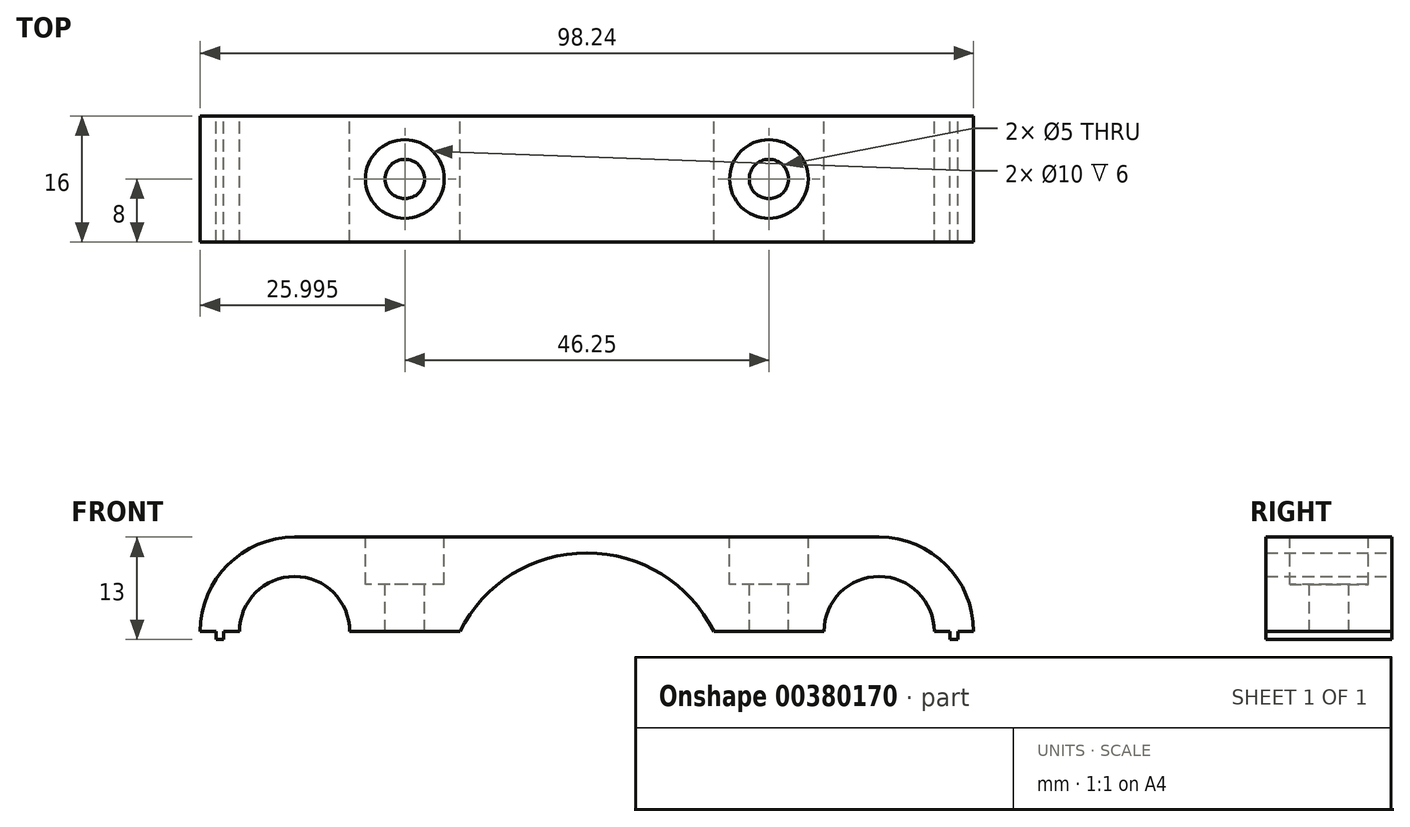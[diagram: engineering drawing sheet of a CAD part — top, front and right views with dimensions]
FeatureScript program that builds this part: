
annotation { "Feature Type Name" : "Feature", "Feature Type Description" : "" }
export const myFeature = defineFeature(function(context is Context, id is Id, definition is map)
    precondition{}
    {
        {
            var Q0;
            Q0=qCreatedBy(makeId("Front.planeOp"),FACE);
            var sketch = newSketch(context, id + "F0", { "sketchPlane" : qUnion([Q0])});
            skLineSegment(sketch, "E0", {"start": v(-44.12, -6) * mm, "end": v(-49.12, -6) * mm});
            skLineSegment(sketch, "E1", {"start": v(-49.12, -6) * mm, "end": v(-49.12, 6) * mm});
            skLineSegment(sketch, "E2", {"start": v(-49.12, 6) * mm, "end": v(49.12, 6) * mm});
            skLineSegment(sketch, "E3", {"start": v(49.12, 6) * mm, "end": v(49.12, -6) * mm});
            skLineSegment(sketch, "E4", {"start": v(49.12, -6) * mm, "end": v(44.12, -6) * mm});
            skArc(sketch, "E5", {"start": v(44.13, -6) * mm, "mid": v(37.13, 1) * mm, "end": v(30.12, -6) * mm});
            skArc(sketch, "E6", {"start": v(-30.12, -6) * mm, "mid": v(-37.12, 1) * mm, "end": v(-44.12, -6) * mm});
            skArc(sketch, "E7", {"start": v(16.12, -6) * mm, "mid": v(0, 4) * mm, "end": v(-16.12, -6) * mm});
            skLineSegment(sketch, "E8", {"start": v(-30.12, -6) * mm, "end": v(-16.12, -6) * mm});
            skLineSegment(sketch, "E9", {"start": v(16.12, -6) * mm, "end": v(30.12, -6) * mm});
            skSolve(sketch);
        }
        {
            var Q0;
            Q0=makeQuery(id+"F0.imprint","IMPRINT",FACE,{"disambiguationData":[TD([[makeQuery(id+"F0.imprint","IMPRINT",EDGE,{"derivedFrom":sQuery(id+"F0.wireOp",EDGE,"E0")}),-1.0]])]});
            extrude(context, id + "F1", {"entities" : qUnion([Q0]), "endBound" : BoundingType.SYMMETRIC, "depth" : 16 * mm});
        }
        {
            var Q0;
            Q0=makeQuery(id+"F1.opExtrude","SWEPT_FACE",FACE,{"disambiguationData":[OSD([sQuery(id+"F0.wireOp",EDGE,"E2")])]});
            var sketch = newSketch(context, id + "F2", { "sketchPlane" : qUnion([Q0])});
            skPoint(sketch, "E10", {"position": v(-23.12, 0) * mm});
            skPoint(sketch, "E11", {"position": v(23.12, 0) * mm});
            skSolve(sketch);
        }
        {
            var Q0;
            Q0=sQuery(id+"F2.wireOp",VERTEX,"c18a094e-cac8-44d5-8395-e5b24407ddbc");
            var Q1;
            Q1=sQuery(id+"F2.wireOp",VERTEX,"E10");
            var Q2;
            Q2=sQuery(id+"F2.wireOp",VERTEX,"E11");
            var Q3;
            Q3=sQuery(id+"F2.wireOp",VERTEX,"e4976973-dec0-4e5f-b838-203971ea5778");
            var Q4;
            Q4=makeQuery(id+"F1.opExtrude","SWEPT_BODY",BODY,{"disambiguationData":[OSD([sQuery(id+"F0.wireOp",EDGE,"E0"),sQuery(id+"F0.wireOp",EDGE,"E1"),sQuery(id+"F0.wireOp",EDGE,"E2"),sQuery(id+"F0.wireOp",EDGE,"E3"),sQuery(id+"F0.wireOp",EDGE,"E4"),sQuery(id+"F0.wireOp",EDGE,"E5"),sQuery(id+"F0.wireOp",EDGE,"E6"),sQuery(id+"F0.wireOp",EDGE,"IZRTLZFC-gH6G-mexX-SaW8-7kCsowfcQd4H")])]});
            hole(context, id + "F3", {"style" : HoleStyle.C_BORE, "endStyle" : HoleEndStyle.THROUGH, "holeDiameter" : 5 * mm, "cBoreDiameter" : 10 * mm, "cBoreDepth" : 6 * mm, "isTappedThrough" : true, "tappedDepth" : 12.7 * mm, "tapClearance" : 3, "locations" : qUnion([Q0, Q1, Q2, Q3]), "scope" : qUnion([Q4])});
        }
        {
            var Q0;
            Q0=makeQuery(id+"F1.opExtrude","SWEPT_EDGE",EDGE,{"disambiguationData":[OSD([sQuery(id+"F0.wireOp",EDGE,"E2"),sQuery(id+"F0.wireOp",EDGE,"E3")])]});
            var Q1;
            Q1=makeQuery(id+"F1.opExtrude","SWEPT_EDGE",EDGE,{"disambiguationData":[OSD([sQuery(id+"F0.wireOp",EDGE,"E1"),sQuery(id+"F0.wireOp",EDGE,"E2")])]});
            fillet(context, id + "F4", {"entities" : qUnion([Q0, Q1]), "radius" : 12 * mm, "tangentPropagation" : true, "allowEdgeOverflow" : false});
        }
        {
            var Q0;
            Q0=makeQuery(id+"F1.opExtrude","SWEPT_FACE",FACE,{"disambiguationData":[OSD([sQuery(id+"F0.wireOp",EDGE,"E0")])]});
            var sketch = newSketch(context, id + "F5", { "sketchPlane" : qUnion([Q0])});
            skLineSegment(sketch, "E12.bottom", {"start": v(-47.12, 8) * mm, "end": v(-46.12, 8) * mm});
            skLineSegment(sketch, "E12.top", {"start": v(-47.12, -8) * mm, "end": v(-46.12, -8) * mm});
            skLineSegment(sketch, "E12.left", {"start": v(-47.12, 8) * mm, "end": v(-47.12, -8) * mm});
            skLineSegment(sketch, "E12.right", {"start": v(-46.12, 8) * mm, "end": v(-46.12, -8) * mm});
            skSolve(sketch);
        }
        {
            var Q0;
            Q0=makeQuery(id+"F5.imprint","IMPRINT",FACE,{"disambiguationData":[TD([[makeQuery(id+"F5.imprint","IMPRINT",EDGE,{"derivedFrom":sQuery(id+"F5.wireOp",EDGE,"E12.bottom")}),1.0]])]});
            extrude(context, id + "F6", {"entities" : qUnion([Q0]), "operationType" : NewBodyOperationType.ADD, "depth" : 1 * mm, "offsetDistance" : 25 * mm});
        }
        {
            var Q0;
            Q0=makeQuery(id+"F1.opExtrude","SWEPT_FACE",FACE,{"disambiguationData":[OSD([sQuery(id+"F0.wireOp",EDGE,"E4")])]});
            var sketch = newSketch(context, id + "F7", { "sketchPlane" : qUnion([Q0])});
            skLineSegment(sketch, "E13.bottom", {"start": v(46.12, 8) * mm, "end": v(47.12, 8) * mm});
            skLineSegment(sketch, "E13.top", {"start": v(46.12, -8) * mm, "end": v(47.12, -8) * mm});
            skLineSegment(sketch, "E13.left", {"start": v(46.12, 8) * mm, "end": v(46.12, -8) * mm});
            skLineSegment(sketch, "E13.right", {"start": v(47.12, 8) * mm, "end": v(47.12, -8) * mm});
            skSolve(sketch);
        }
        {
            var Q0;
            Q0=makeQuery(id+"F7.imprint","IMPRINT",FACE,{"disambiguationData":[TD([[makeQuery(id+"F7.imprint","IMPRINT",EDGE,{"derivedFrom":sQuery(id+"F7.wireOp",EDGE,"E13.bottom")}),1.0]])]});
            extrude(context, id + "F8", {"entities" : qUnion([Q0]), "operationType" : NewBodyOperationType.ADD, "depth" : 1 * mm, "offsetDistance" : 25 * mm});
        }
    });
